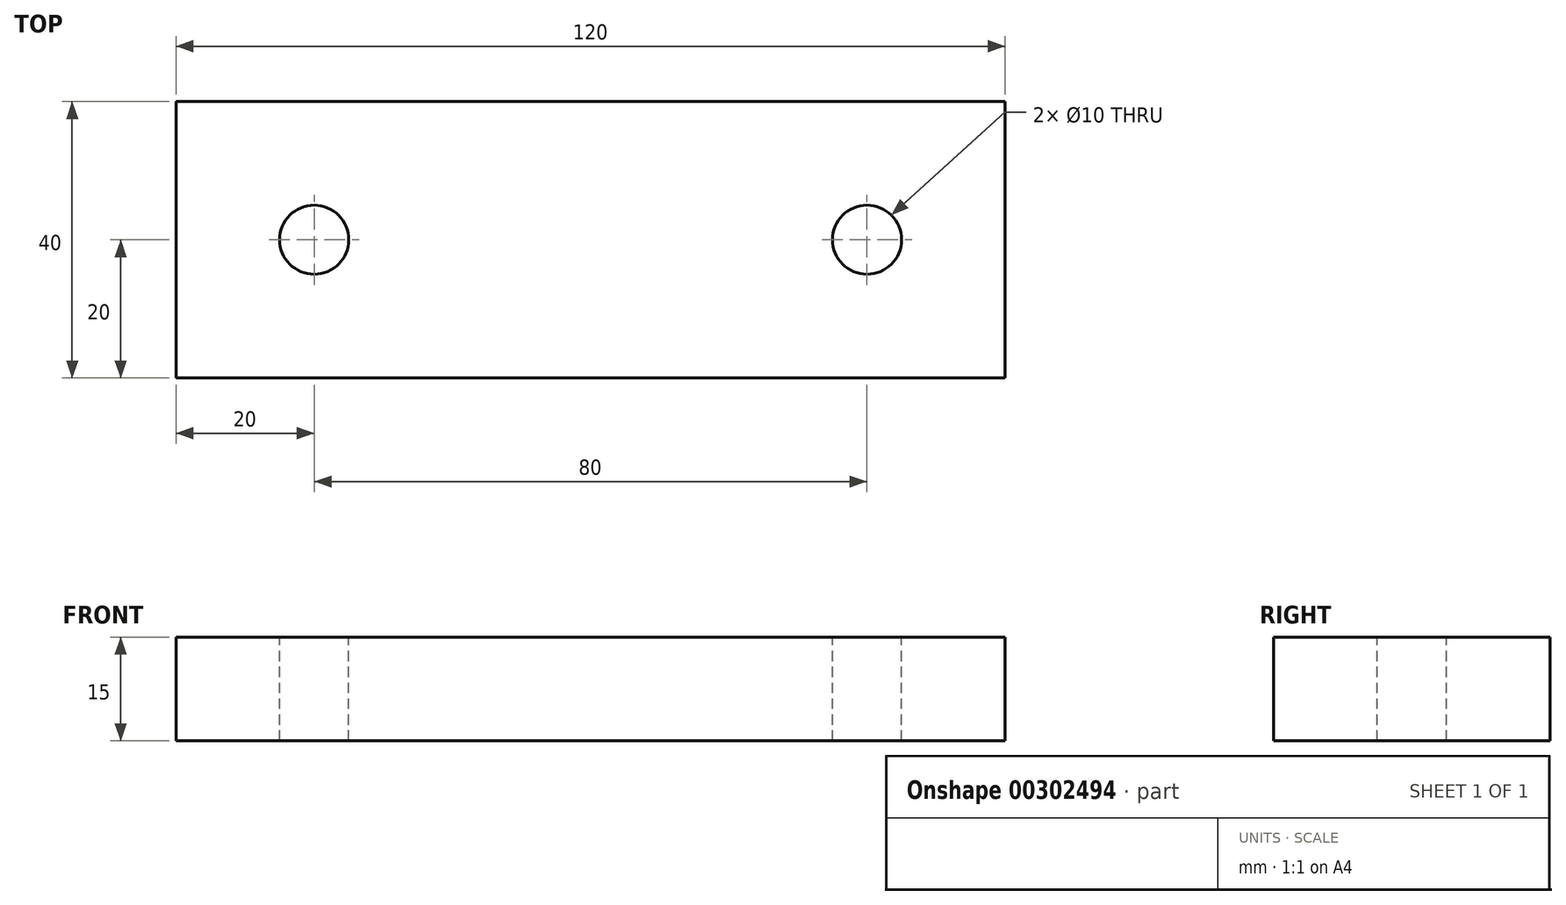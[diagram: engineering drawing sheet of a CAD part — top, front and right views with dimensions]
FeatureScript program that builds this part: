
annotation { "Feature Type Name" : "Feature", "Feature Type Description" : "" }
export const myFeature = defineFeature(function(context is Context, id is Id, definition is map)
    precondition{}
    {
        {
            var Q0;
            Q0=qCreatedBy(makeId("Front.planeOp"),FACE);
            var sketch = newSketch(context, id + "F0", { "sketchPlane" : qUnion([Q0])});
            skLineSegment(sketch, "E0", {"start": v(0, 0) * mm, "end": v(120, 0) * mm});
            skLineSegment(sketch, "E1", {"start": v(120, 0) * mm, "end": v(120, 15) * mm});
            skLineSegment(sketch, "E2", {"start": v(120, 15) * mm, "end": v(0, 15) * mm});
            skLineSegment(sketch, "E3", {"start": v(0, 15) * mm, "end": v(0, 0) * mm});
            skSolve(sketch);
        }
        {
            var Q0;
            Q0=makeQuery(id+"F0.imprint","IMPRINT",FACE,{"disambiguationData":[TD([[makeQuery(id+"F0.imprint","IMPRINT",EDGE,{"derivedFrom":sQuery(id+"F0.wireOp",EDGE,"E0")}),1.0]])]});
            extrude(context, id + "F1", {"entities" : qUnion([Q0]), "depth" : 40 * mm, "symmetric" : true});
        }
        {
            var Q0;
            Q0=makeQuery(id+"F1.opExtrude","SWEPT_FACE",FACE,{"disambiguationData":[OSD([sQuery(id+"F0.wireOp",EDGE,"E2")])]});
            var sketch = newSketch(context, id + "F2", { "sketchPlane" : qUnion([Q0])});
            skCircle(sketch, "E4", {"center": v(20, 0) * mm, "radius": 5 * mm});
            skCircle(sketch, "E5", {"center": v(100, 0) * mm, "radius": 5 * mm});
            skSolve(sketch);
        }
        {
            var Q0;
            Q0=makeQuery(id+"F2.imprint","IMPRINT",FACE,{"disambiguationData":[TD([[makeQuery(id+"F2.imprint","IMPRINT",EDGE,{"derivedFrom":sQuery(id+"F2.wireOp",EDGE,"E4")}),1.0]])]});
            var Q1;
            Q1=makeQuery(id+"F2.imprint","IMPRINT",FACE,{"disambiguationData":[TD([[makeQuery(id+"F2.imprint","IMPRINT",EDGE,{"derivedFrom":sQuery(id+"F2.wireOp",EDGE,"E5")}),1.0]])]});
            extrude(context, id + "F3", {"entities" : qUnion([Q0, Q1]), "operationType" : NewBodyOperationType.REMOVE, "endBound" : BoundingType.THROUGH_ALL, "oppositeDirection" : true, "depth" : 25 * mm});
        }
    });
